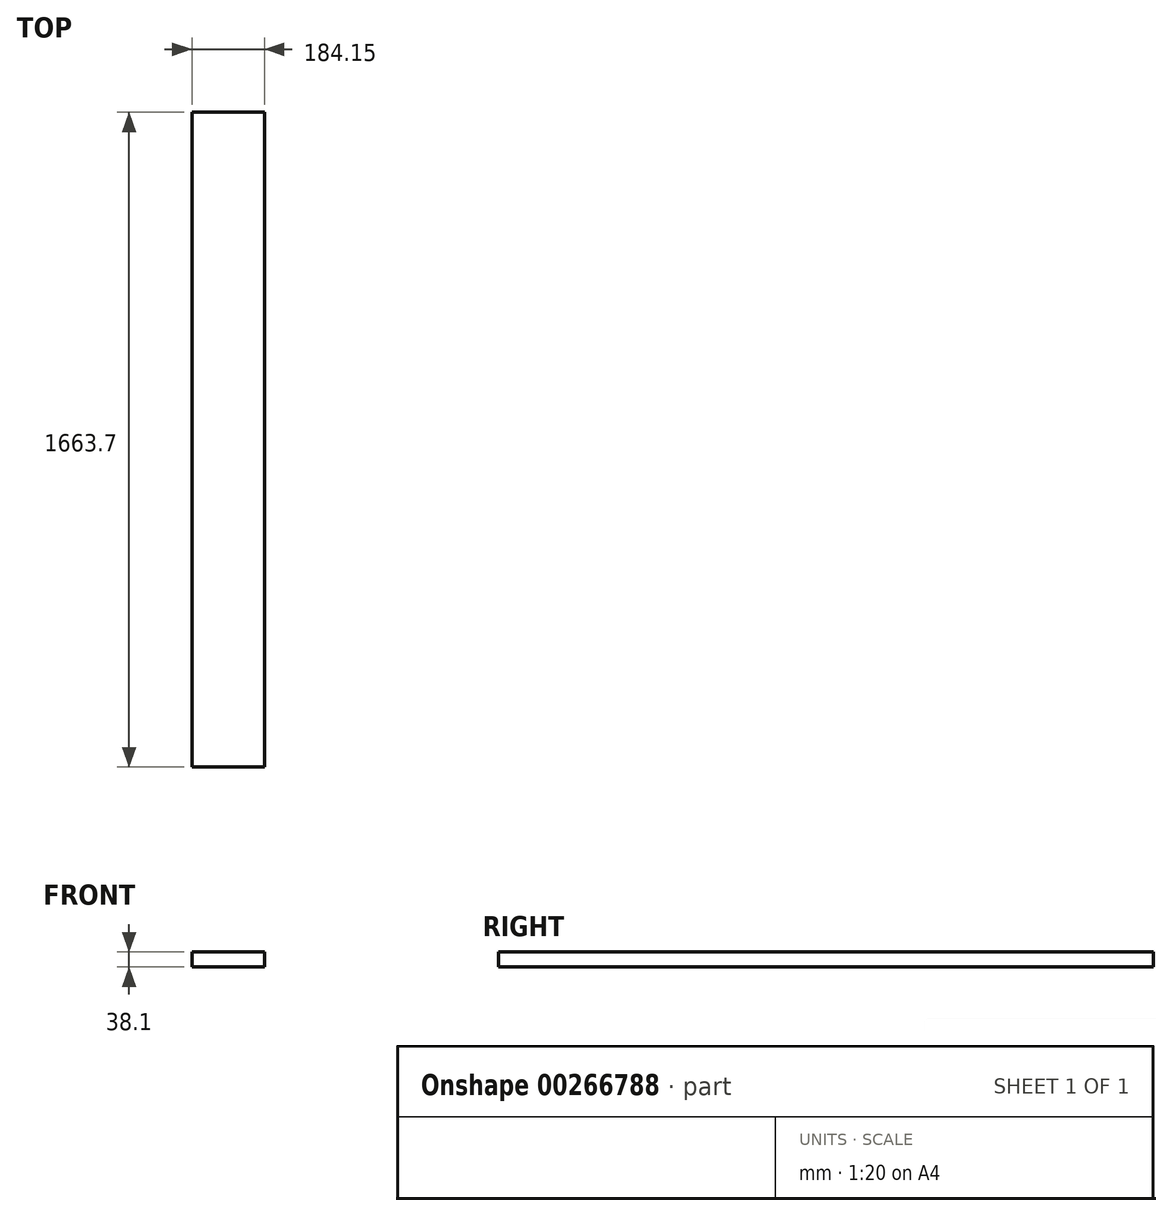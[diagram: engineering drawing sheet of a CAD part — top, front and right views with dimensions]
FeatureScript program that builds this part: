
annotation { "Feature Type Name" : "Feature", "Feature Type Description" : "" }
export const myFeature = defineFeature(function(context is Context, id is Id, definition is map)
    precondition{}
    {
        {
            var Q0;
            Q0=qCreatedBy(makeId("Front.planeOp"),FACE);
            var sketch = newSketch(context, id + "F0", { "sketchPlane" : qUnion([Q0])});
            skLineSegment(sketch, "E0.bottom", {"start": v(-48.34, 23.68) * mm, "end": v(135.8, 23.68) * mm});
            skLineSegment(sketch, "E0.top", {"start": v(-48.34, -14.42) * mm, "end": v(135.8, -14.42) * mm});
            skLineSegment(sketch, "E0.left", {"start": v(-48.34, 23.68) * mm, "end": v(-48.34, -14.42) * mm});
            skLineSegment(sketch, "E0.right", {"start": v(135.8, 23.68) * mm, "end": v(135.8, -14.42) * mm});
            skSolve(sketch);
        }
        {
            var Q0;
            Q0=qSketchRegion(id+"F0",true);
            extrude(context, id + "F1", {"entities" : qUnion([Q0]), "depth" : 1663.7 * mm});
        }
    });
